# Revit family: CONV_Flokk_DmstcChrs_HAGConventioWing9811
name_source: partatom
category: Furniture
revit_build: Autodesk Revit 2015 (Build: 20140606_1530(x64)
units: mm (PartAtom-declared; Revit-internal decimal feet)

## types (1)
- CONV_Flokk_DmstcChrs_HAGConventioWing9811
    AssetType = Movable
    BIMObjectName = CONV_Flokk_DmstcChrs_HAGConventioWing9811
    Brand = HAG
    Category = Meeting chairs
    Collection = HAG Conventio Wing
    Color = Various
    ConvergoRefNr = 0119-1802-0018-NO
    Cost = 0 $
    Designer = Peter Opsvik
    DurationUnit = Year
    ExpiringDate = 08/2018
    Features = Stackable 15 high
    HighestSeatingHeight = 440 mm
    IfcExportAs = IfcFurnishingElementType
    IfcExportType = CHAIR
    LowestSeatingHeight = 440 mm
    MainColor = Various
    Manufacturer = Flokk
    ManufacturerName = Flokk
    ManufacturerURL = https://www.flokk.com
    Material = Plastic, aluminum
    Model = HAG Conventio Wing 9811
    ModelNumber = 9811
    NBSDescription = Stacking chairs
    NBSReference = 45-35-20/355
    Name = DmstcChrs_HAGConventioWing9811
    NominalDepth = 588 mm
    NominalHeight = 900 mm  [stored 2.95276 ft]
    NominalLength = 524 mm
    OfficeChairTertiaryMaterial = Plastic, Opaque Black
    ProductInformation = The HÅG Conventio Wing 9811 is a self-stabilizing, lightweight chair that is easily to set out and stack away. The chairs can be stacked fifteen high. HÅG in Balance® technology ensures more subconscious movement. Armrests and the HÅG Writing Tablet available as optional extras.
    SeatingHeight = 440 mm
    Shape = Sculptured
    Size = 524x590x900 mm
    URL = https://www.flokk.com
    Uniclass2 = Pr_40_50_12_51
    Uniclass2015Description = Meeting room chairs
    Uniclass2015Reference = Pr_40_50_12_51
    Version = 1
    VersionDate = 23/03/2018
    WarrantyDurationUnit = Year
    Weight = 5.2 kg

note: [stored X ft] marks values corroborated as IEEE doubles in the binary element streams (Revit-internal decimal feet)

## geometry (parser evidence)
native form markers: Blend x4, Sweep x6
no freeform markers — native parametric forms only
